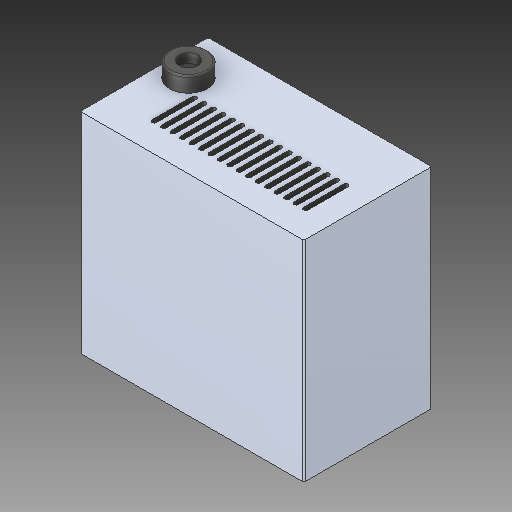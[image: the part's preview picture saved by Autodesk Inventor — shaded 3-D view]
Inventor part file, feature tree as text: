
AUTODESK INVENTOR PART (.ipt)
format: ipt  version: 2018 (Build 220112000, 112)  size: 1,050,112 bytes
history: mixed  units: mm
features: sketch x3, extrude x3, fillet x1, imported_body x1
ambient origin geometry x8: Origin, YZ Plane, XZ Plane, XY Plane, X Axis, Y Axis, Z Axis, Center Point
bodies: Solid1 (imported_parasolid)
feature tree (8):
  sketch  "Sketch1"  dims[d0=6.0mm d1=5.0mm]
  extrude  "Extrusion1"  Depth=5.0mm
  extrude  "Extrusion2"  Depth=6.0mm
  extrude  "Extrusion3"  Depth=10.0mm
  sketch  "Sketch2"  dims[d2=3.0mm d3=6.0mm]
  sketch  "Sketch3"  dims[d4=17.0mm d5=30.0mm d6=6.0mm d7=6.0mm d8=5.0mm d9=3.0mm d10=3.0mm d11=3.0mm d12=10.0mm d13=0.0mm d14=10.0mm d15=0.0mm d16=10.0mm d17=0.0mm]
  fillet  "Fillet3"  Radius=6.0mm
  imported_body  NMx_Import_Brep_tag  [imported B-rep: ~32 faces, bbox_mm=[149.86, 140.462, 85.725]]
